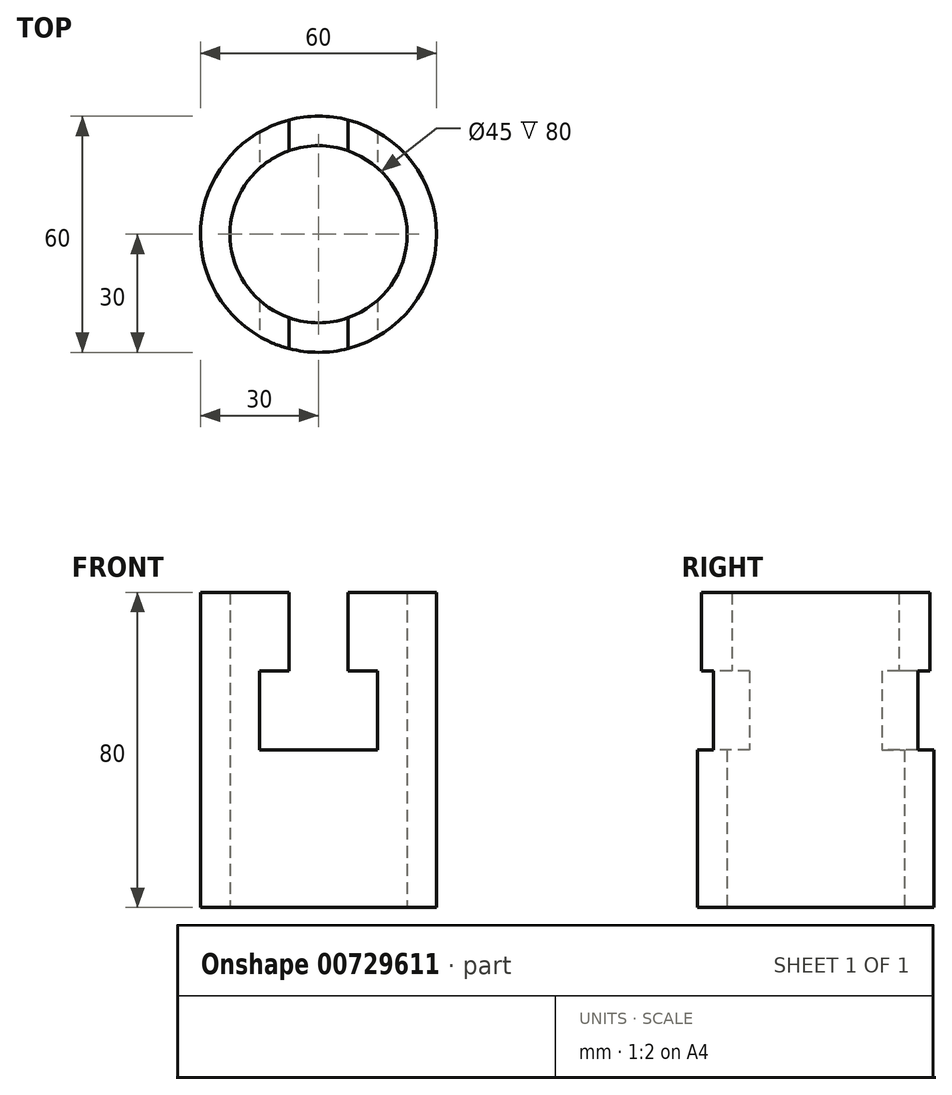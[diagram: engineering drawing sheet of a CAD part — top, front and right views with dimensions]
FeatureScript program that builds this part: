
annotation { "Feature Type Name" : "Feature", "Feature Type Description" : "" }
export const myFeature = defineFeature(function(context is Context, id is Id, definition is map)
    precondition{}
    {
        {
            var Q0;
            Q0=qCreatedBy(makeId("Top.planeOp"),FACE);
            var sketch = newSketch(context, id + "F0", { "sketchPlane" : qUnion([Q0])});
            skCircle(sketch, "E0", {"center": v(0, 0) * mm, "radius": 30 * mm});
            skCircle(sketch, "E1", {"center": v(0, 0) * mm, "radius": 22.5 * mm});
            skSolve(sketch);
        }
        {
            var Q0;
            Q0=makeQuery(id+"F0.imprint","IMPRINT",FACE,{"disambiguationData":[TD([[makeQuery(id+"F0.imprint","IMPRINT",EDGE,{"derivedFrom":sQuery(id+"F0.wireOp",EDGE,"E0")}),1.0]])]});
            extrude(context, id + "F1", {"entities" : qUnion([Q0]), "depth" : 80 * mm, "offsetDistance" : 25 * mm});
        }
        {
            var Q0;
            Q0=qCreatedBy(makeId("Front.planeOp"),FACE);
            var sketch = newSketch(context, id + "F2", { "sketchPlane" : qUnion([Q0])});
            skLineSegment(sketch, "E2.bottom", {"start": v(-15, 60) * mm, "end": v(-7.5, 60) * mm});
            skLineSegment(sketch, "E2.top", {"start": v(-15, 40) * mm, "end": v(15, 40) * mm});
            skLineSegment(sketch, "E2.left", {"start": v(-15, 60) * mm, "end": v(-15, 40) * mm});
            skLineSegment(sketch, "E2.right", {"start": v(15, 60) * mm, "end": v(15, 40) * mm});
            skLineSegment(sketch, "E3", {"start": v(-7.5, 60) * mm, "end": v(-7.5, 80) * mm});
            skLineSegment(sketch, "E4", {"start": v(-7.5, 80) * mm, "end": v(7.5, 80) * mm});
            skLineSegment(sketch, "E5", {"start": v(7.5, 80) * mm, "end": v(7.5, 60) * mm});
            skLineSegment(sketch, "E6.trimOffspring", {"start": v(7.5, 60) * mm, "end": v(15, 60) * mm});
            skSolve(sketch);
        }
        {
            var Q0;
            Q0=makeQuery(id+"F2.imprint","IMPRINT",FACE,{"disambiguationData":[TD([[makeQuery(id+"F2.imprint","IMPRINT",EDGE,{"derivedFrom":sQuery(id+"F2.wireOp",EDGE,"E2.bottom")}),-1.0]])]});
            extrude(context, id + "F3", {"entities" : qUnion([Q0]), "operationType" : NewBodyOperationType.REMOVE, "endBound" : BoundingType.SYMMETRIC, "oppositeDirection" : true, "depth" : 60 * mm, "offsetDistance" : 25 * mm});
        }
    });
